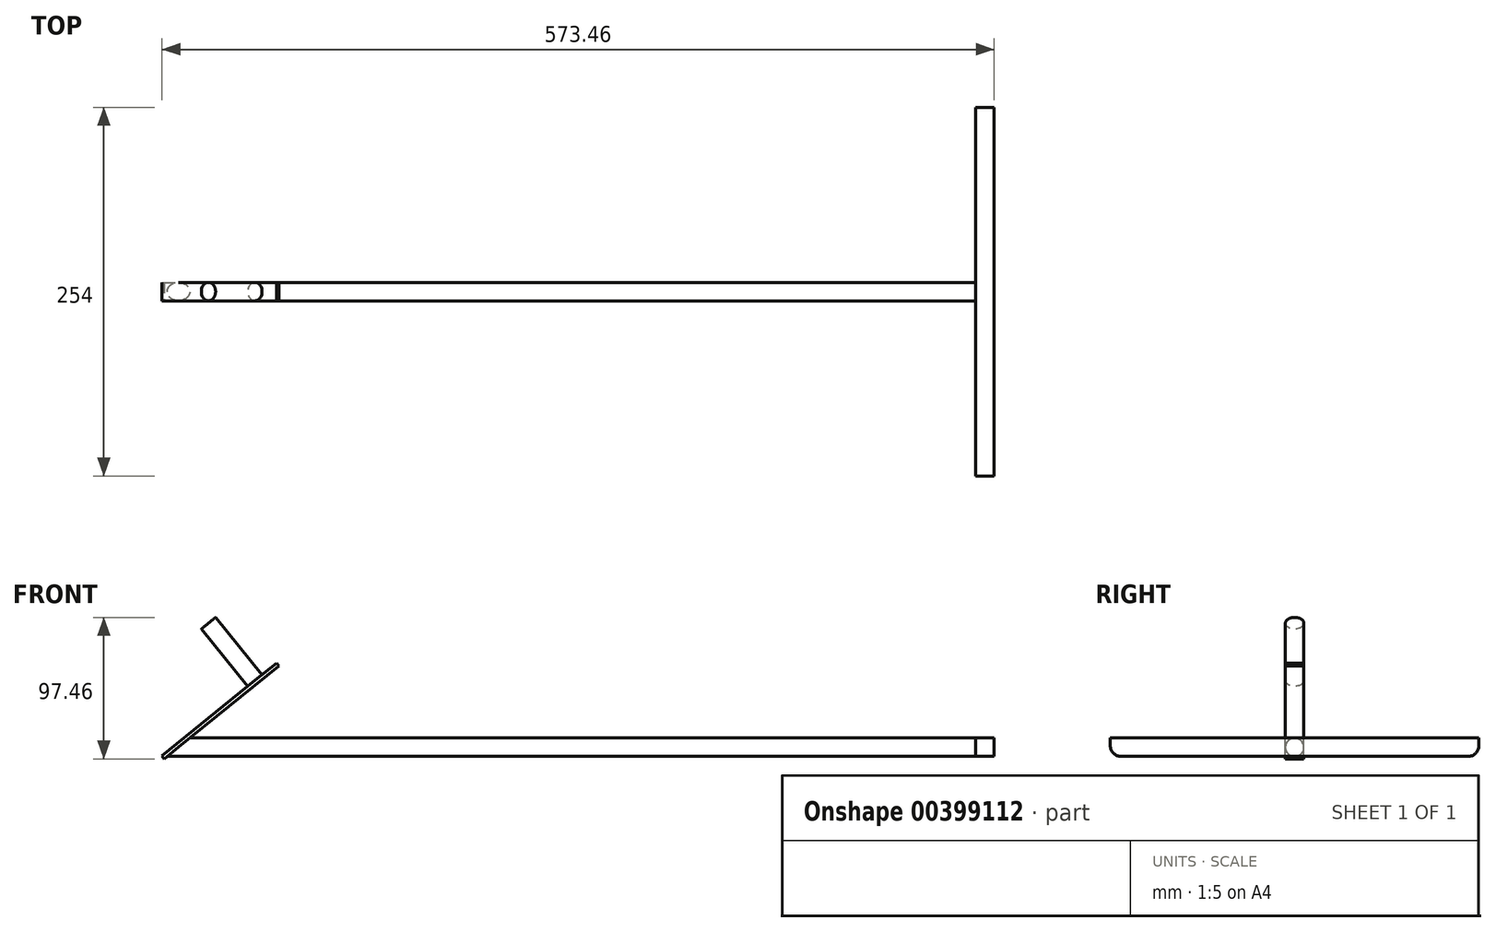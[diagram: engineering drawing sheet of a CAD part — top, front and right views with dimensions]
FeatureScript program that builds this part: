
annotation { "Feature Type Name" : "Feature", "Feature Type Description" : "" }
export const myFeature = defineFeature(function(context is Context, id is Id, definition is map)
    precondition{}
    {
        {
            var Q0;
            Q0=qCreatedBy(makeId("Right.planeOp"),FACE);
            var sketch = newSketch(context, id + "F0", { "sketchPlane" : qUnion([Q0])});
            skLineSegment(sketch, "E0.bottom", {"start": v(-127, -6.35) * mm, "end": v(127, -6.35) * mm});
            skLineSegment(sketch, "E0.top", {"start": v(-127, 6.35) * mm, "end": v(127, 6.35) * mm});
            skLineSegment(sketch, "E0.left", {"start": v(-127, -6.35) * mm, "end": v(-127, 6.35) * mm});
            skLineSegment(sketch, "E0.right", {"start": v(127, -6.35) * mm, "end": v(127, 6.35) * mm});
            skPoint(sketch, "E0.middle", {"position": v(0, 0) * mm});
            skSolve(sketch);
        }
        {
            var Q0;
            Q0=qSketchRegion(id+"F0",true);
            extrude(context, id + "F1", {"entities" : qUnion([Q0]), "depth" : 12.7 * mm});
        }
        {
            var Q0;
            Q0=makeQuery(id+"F1.opExtrude","CAP_FACE",FACE,{"disambiguationData":[OSD([sQuery(id+"F0.wireOp",EDGE,"E0.bottom"),sQuery(id+"F0.wireOp",EDGE,"E0.top"),sQuery(id+"F0.wireOp",EDGE,"E0.left"),sQuery(id+"F0.wireOp",EDGE,"E0.right")])],"isStart":true});
            var sketch = newSketch(context, id + "F2", { "sketchPlane" : qUnion([Q0])});
            skCircle(sketch, "E1", {"center": v(0, 0) * mm, "radius": 6.35 * mm});
            skSolve(sketch);
        }
        {
            var Q0;
            {var subQ0=sQuery(id+"F2.wireOp",EDGE,"E1");var subQ1=makeQuery(id+"F2.imprint","INTERSECT",VERTEX,{"derivedFrom":[makeQuery(id+"F1.opExtrude","CAP_EDGE",EDGE,{"disambiguationData":[OSD([sQuery(id+"F0.wireOp",EDGE,"E0.bottom")])],"isStart":true}),subQ0]});Q0=makeQuery(id+"F2.imprint","IMPRINT",FACE,{"disambiguationData":[TD([[makeQuery(id+"F2.imprint","IMPRINT",EDGE,{"disambiguationData":[TD([[subQ1,1.0]])],"derivedFrom":subQ0}),1.0]])]});}
            extrude(context, id + "F3", {"entities" : qUnion([Q0]), "operationType" : NewBodyOperationType.ADD, "depth" : 558.8 * mm});
        }
        {
            var Q0;
            Q0=makeQuery(id+"FupoaZT84nc10jQ_1.boolean.opBoolean","MERGE",EDGE,{"derivedFrom":[makeQuery(id+"F1.opExtrude","SWEPT_EDGE",EDGE,{"disambiguationData":[OSD([sQuery(id+"F0.wireOp",EDGE,"E0.bottom"),sQuery(id+"F0.wireOp",EDGE,"E0.right")])]}),makeQuery(id+"FupoaZT84nc10jQ_1.opExtrude","SWEPT_EDGE",EDGE,{"disambiguationData":[OSD([sQuery(id+"FkZ35c0B0zU1X3f_1.wireOp",EDGE,"WDlY2Xsi-TDD2-VCIr-D7En-CllaiiGBWpdX.bottom"),sQuery(id+"FkZ35c0B0zU1X3f_1.wireOp",EDGE,"WDlY2Xsi-TDD2-VCIr-D7En-CllaiiGBWpdX.left")])]})]});
            var Q1;
            Q1=makeQuery(id+"FupoaZT84nc10jQ_1.opExtrude","SWEPT_EDGE",EDGE,{"disambiguationData":[OSD([sQuery(id+"F0.wireOp",EDGE,"E0.bottom"),sQuery(id+"FkZ35c0B0zU1X3f_1.wireOp",EDGE,"WDlY2Xsi-TDD2-VCIr-D7En-CllaiiGBWpdX.bottom"),sQuery(id+"FkZ35c0B0zU1X3f_1.wireOp",EDGE,"WDlY2Xsi-TDD2-VCIr-D7En-CllaiiGBWpdX.right")])]});
            var Q2;
            Q2=makeQuery(id+"Fi0yoORkA4mHtm4_1.opExtrude","SWEPT_EDGE",EDGE,{"disambiguationData":[OSD([sQuery(id+"F0.wireOp",EDGE,"E0.bottom"),sQuery(id+"FWHJNf8wGArpJ2s_1.wireOp",EDGE,"LEykWHhn-yVjQ-QP4P-oKNU-XplFAZDmla1z.bottom"),sQuery(id+"FWHJNf8wGArpJ2s_1.wireOp",EDGE,"LEykWHhn-yVjQ-QP4P-oKNU-XplFAZDmla1z.right")])]});
            var Q3;
            Q3=makeQuery(id+"Fi0yoORkA4mHtm4_1.boolean.opBoolean","MERGE",EDGE,{"derivedFrom":[makeQuery(id+"F1.opExtrude","SWEPT_EDGE",EDGE,{"disambiguationData":[OSD([sQuery(id+"F0.wireOp",EDGE,"E0.bottom"),sQuery(id+"F0.wireOp",EDGE,"E0.left")])]}),makeQuery(id+"Fi0yoORkA4mHtm4_1.opExtrude","SWEPT_EDGE",EDGE,{"disambiguationData":[OSD([sQuery(id+"FWHJNf8wGArpJ2s_1.wireOp",EDGE,"LEykWHhn-yVjQ-QP4P-oKNU-XplFAZDmla1z.bottom"),sQuery(id+"FWHJNf8wGArpJ2s_1.wireOp",EDGE,"LEykWHhn-yVjQ-QP4P-oKNU-XplFAZDmla1z.left")])]})]});
            fillet(context, id + "F4", {"entities" : qUnion([Q0, Q1, Q2, Q3]), "radius" : 7.62 * mm, "tangentPropagation" : true, "allowEdgeOverflow" : false});
        }
        {
            var Q0;
            Q0=qCreatedBy(makeId("Front.planeOp"),FACE);
            var sketch = newSketch(context, id + "F5", { "sketchPlane" : qUnion([Q0])});
            skLineSegment(sketch, "E2", {"start": v(-558.8, 6.7) * mm, "end": v(-558.8, -7.68) * mm});
            skLineSegment(sketch, "E3", {"start": v(-558.8, -7.68) * mm, "end": v(-541.1, 6.7) * mm});
            skLineSegment(sketch, "E4", {"start": v(-541.1, 6.7) * mm, "end": v(-558.8, 6.7) * mm});
            skSolve(sketch);
        }
        {
            var Q0;
            Q0=qSketchRegion(id+"F5",true);
            extrude(context, id + "F6", {"entities" : qUnion([Q0]), "operationType" : NewBodyOperationType.REMOVE, "endBound" : BoundingType.SYMMETRIC, "oppositeDirection" : true, "depth" : 25.4 * mm});
        }
        {
            var Q0;
            Q0=makeQuery(id+"F6.boolean.opBoolean","COPY",FACE,{"derivedFrom":makeQuery(id+"F6.opExtrude","SWEPT_FACE",FACE,{"disambiguationData":[OSD([sQuery(id+"F5.wireOp",EDGE,"E3")])]})});
            var sketch = newSketch(context, id + "F7", { "sketchPlane" : qUnion([Q0])});
            skPoint(sketch, "E5.oppositeSnap0", {"position": v(-426.35, -6.35) * mm});
            skLineSegment(sketch, "E5.bottom", {"start": v(-439, 6.35) * mm, "end": v(-337.4, 6.35) * mm});
            skLineSegment(sketch, "E5.top", {"start": v(-439, -6.35) * mm, "end": v(-337.4, -6.35) * mm});
            skLineSegment(sketch, "E5.left", {"start": v(-439, 6.35) * mm, "end": v(-439, -6.35) * mm});
            skLineSegment(sketch, "E5.right", {"start": v(-337.4, 6.35) * mm, "end": v(-337.4, -6.35) * mm});
            skSolve(sketch);
        }
        {
            var Q0;
            Q0=qSketchRegion(id+"F7",true);
            extrude(context, id + "F8", {"entities" : qUnion([Q0]), "operationType" : NewBodyOperationType.ADD, "depth" : 2.54 * mm});
        }
        {
            var Q0;
            Q0=makeQuery(id+"F8.opExtrude","CAP_FACE",FACE,{"disambiguationData":[OSD([sQuery(id+"F7.wireOp",EDGE,"E5.bottom"),sQuery(id+"F7.wireOp",EDGE,"E5.top"),sQuery(id+"F7.wireOp",EDGE,"E5.left"),sQuery(id+"F7.wireOp",EDGE,"E5.right")])],"isStart":false});
            var sketch = newSketch(context, id + "F9", { "sketchPlane" : qUnion([Q0])});
            skCircle(sketch, "E6", {"center": v(-356.44, 0) * mm, "radius": 6.35 * mm});
            skSolve(sketch);
        }
        {
            var Q0;
            {var subQ0=sQuery(id+"F9.wireOp",EDGE,"E6");var subQ1=makeQuery(id+"F9.imprint","INTERSECT",VERTEX,{"derivedFrom":[makeQuery(id+"F8.opExtrude","CAP_EDGE",EDGE,{"disambiguationData":[OSD([sQuery(id+"F7.wireOp",EDGE,"E5.bottom")])],"isStart":false}),subQ0]});Q0=makeQuery(id+"F9.imprint","IMPRINT",FACE,{"disambiguationData":[TD([[makeQuery(id+"F9.imprint","IMPRINT",EDGE,{"disambiguationData":[TD([[subQ1,-1.0]])],"derivedFrom":subQ0}),1.0]])]});}
            extrude(context, id + "F10", {"entities" : qUnion([Q0]), "operationType" : NewBodyOperationType.ADD, "depth" : 50.8 * mm});
        }
    });
